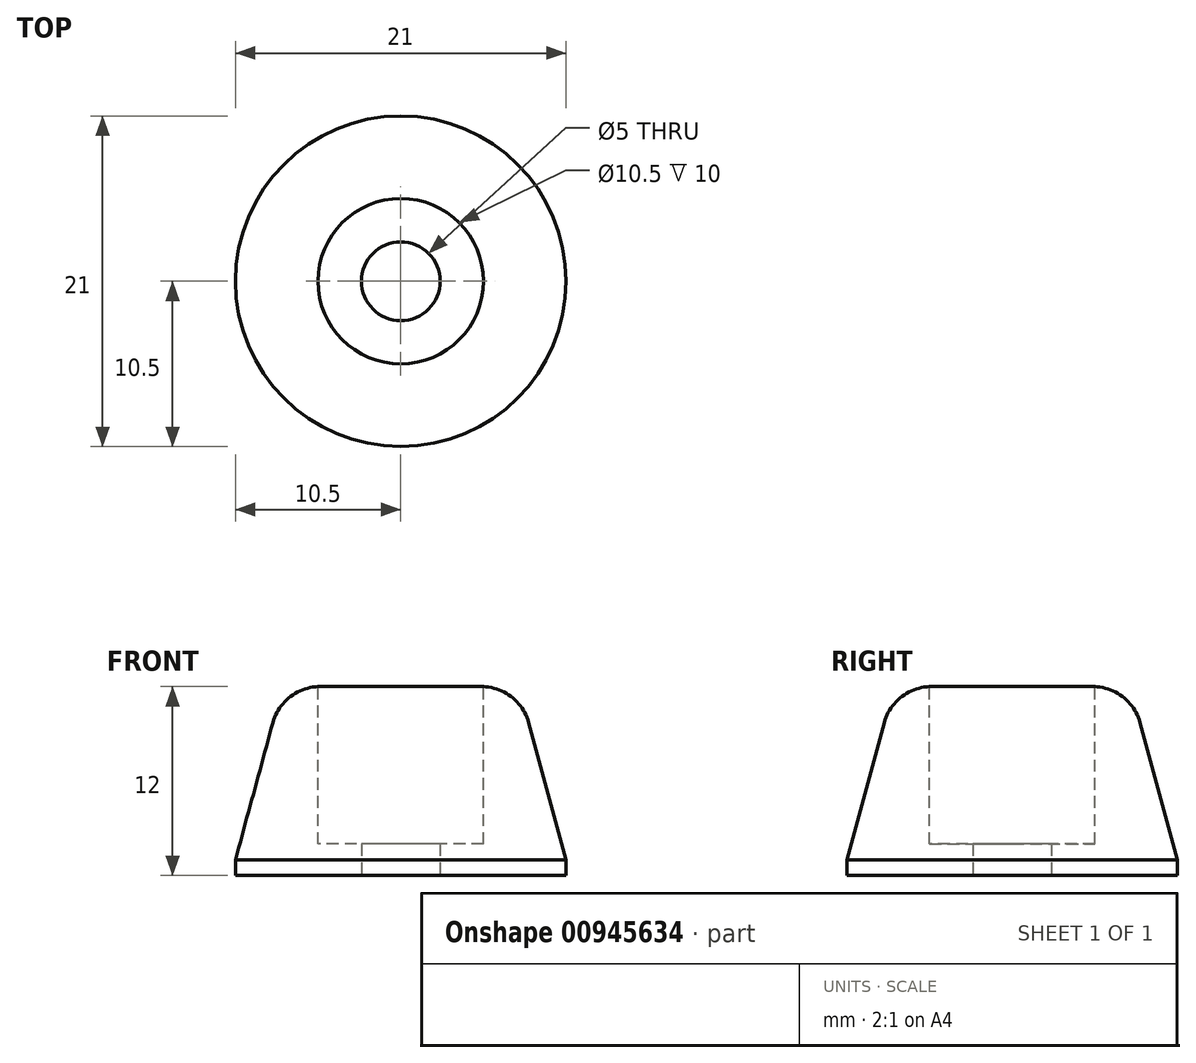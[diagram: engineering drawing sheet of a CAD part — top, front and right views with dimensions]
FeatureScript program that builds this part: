
annotation { "Feature Type Name" : "Feature", "Feature Type Description" : "" }
export const myFeature = defineFeature(function(context is Context, id is Id, definition is map)
    precondition{}
    {
        {
            var Q0;
            Q0=qCreatedBy(makeId("Top.planeOp"),FACE);
            var sketch = newSketch(context, id + "F0", { "sketchPlane" : qUnion([Q0])});
            skCircle(sketch, "E0", {"center": v(0, 0) * mm, "radius": 10.5 * mm});
            skSolve(sketch);
        }
        {
            var Q0;
            Q0=makeQuery(id+"F0.imprint","IMPRINT",FACE,{"disambiguationData":[TD([[makeQuery(id+"F0.imprint","IMPRINT",EDGE,{"derivedFrom":sQuery(id+"F0.wireOp",EDGE,"E0")}),1.0]])]});
            extrude(context, id + "F1", {"entities" : qUnion([Q0]), "depth" : 1 * mm, "offsetDistance" : 25 * mm});
        }
        {
            var Q0;
            Q0=qCreatedBy(makeId("Top.planeOp"),FACE);
            cPlane(context, id + "F2", {"entities" : qUnion([Q0]), "cplaneType" : CPlaneType.OFFSET, "offset" : 12 * mm, "width" : 150 * mm, "height" : 150 * mm});
        }
        {
            var Q0;
            Q0=qCreatedBy(id+"F2.planeOp",FACE);
            var sketch = newSketch(context, id + "F3", { "sketchPlane" : qUnion([Q0])});
            skCircle(sketch, "E1", {"center": v(0, 0) * mm, "radius": 7.5 * mm});
            skSolve(sketch);
        }
        {
            var Q1;
            Q1=makeQuery(id+"F1.opExtrude","CAP_FACE",FACE,{"disambiguationData":[OSD([sQuery(id+"F0.wireOp",EDGE,"E0")])],"isStart":false});
            var Q2;
            Q2=makeQuery(id+"F3.imprint","IMPRINT",FACE,{"disambiguationData":[TD([[makeQuery(id+"F3.imprint","IMPRINT",EDGE,{"derivedFrom":sQuery(id+"F3.wireOp",EDGE,"E1")}),1.0]])]});
            loft(context, id + "F4", {"operationType" : NewBodyOperationType.ADD, "sheetProfilesArray" : [{ "sheetProfileEntities" : qUnion([Q1]) }, { "sheetProfileEntities" : qUnion([Q2]) }]});
        }
        {
            var Q0;
            Q0=qCreatedBy(makeId("Top.planeOp"),FACE);
            var sketch = newSketch(context, id + "F5", { "sketchPlane" : qUnion([Q0])});
            skCircle(sketch, "E2", {"center": v(0, 0) * mm, "radius": 2.5 * mm});
            skSolve(sketch);
        }
        {
            var Q0;
            Q0=makeQuery(id+"F5.imprint","IMPRINT",FACE,{"disambiguationData":[TD([[makeQuery(id+"F5.imprint","IMPRINT",EDGE,{"derivedFrom":sQuery(id+"F5.wireOp",EDGE,"E2")}),1.0]])]});
            var Q1;
            Q1=makeQuery(id+"F4.opLoft","CAP_FACE",FACE,{"disambiguationData":[OSD([makeQuery(id+"F3.imprint","IMPRINT",FACE,{"disambiguationData":[TD([[makeQuery(id+"F3.imprint","IMPRINT",EDGE,{"derivedFrom":sQuery(id+"F3.wireOp",EDGE,"E1")}),1.0]])]})])],"isStart":true});
            var Q2;
            Q2=makeQuery(id+"F4.opLoft","CAP_FACE",FACE,{"disambiguationData":[OSD([makeQuery(id+"F3.imprint","IMPRINT",FACE,{"disambiguationData":[TD([[makeQuery(id+"F3.imprint","IMPRINT",EDGE,{"derivedFrom":sQuery(id+"F3.wireOp",EDGE,"E1")}),1.0]])]})])],"isStart":true});
            extrude(context, id + "F6", {"entities" : qUnion([Q0]), "operationType" : NewBodyOperationType.REMOVE, "endBound" : BoundingType.UP_TO_SURFACE, "depth" : 50 * mm, "endBoundEntityFace" : qUnion([Q1]), "offsetDistance" : 25 * mm});
        }
        {
            var Q0;
            Q0=qCreatedBy(id+"F2.planeOp",FACE);
            var sketch = newSketch(context, id + "F7", { "sketchPlane" : qUnion([Q0])});
            skCircle(sketch, "E3", {"center": v(0, 0) * mm, "radius": 5.25 * mm});
            skSolve(sketch);
        }
        {
            var Q0;
            Q0=makeQuery(id+"F7.imprint","IMPRINT",FACE,{"disambiguationData":[TD([[makeQuery(id+"F7.imprint","IMPRINT",EDGE,{"derivedFrom":sQuery(id+"F7.wireOp",EDGE,"E3")}),1.0]])]});
            extrude(context, id + "F8", {"entities" : qUnion([Q0]), "operationType" : NewBodyOperationType.REMOVE, "oppositeDirection" : true, "depth" : 10 * mm, "offsetDistance" : 25 * mm});
        }
        {
            var Q0;
            Q0=makeQuery(id+"F4.opLoft","MID_CAP_EDGE",EDGE,{"disambiguationData":[OSD([sQuery(id+"F3.wireOp",EDGE,"E1")])],"capPos":1.0});
            fillet(context, id + "F9", {"entities" : qUnion([Q0]), "radius" : 3.1 * mm, "tangentPropagation" : true, "allowEdgeOverflow" : false});
        }
    });
